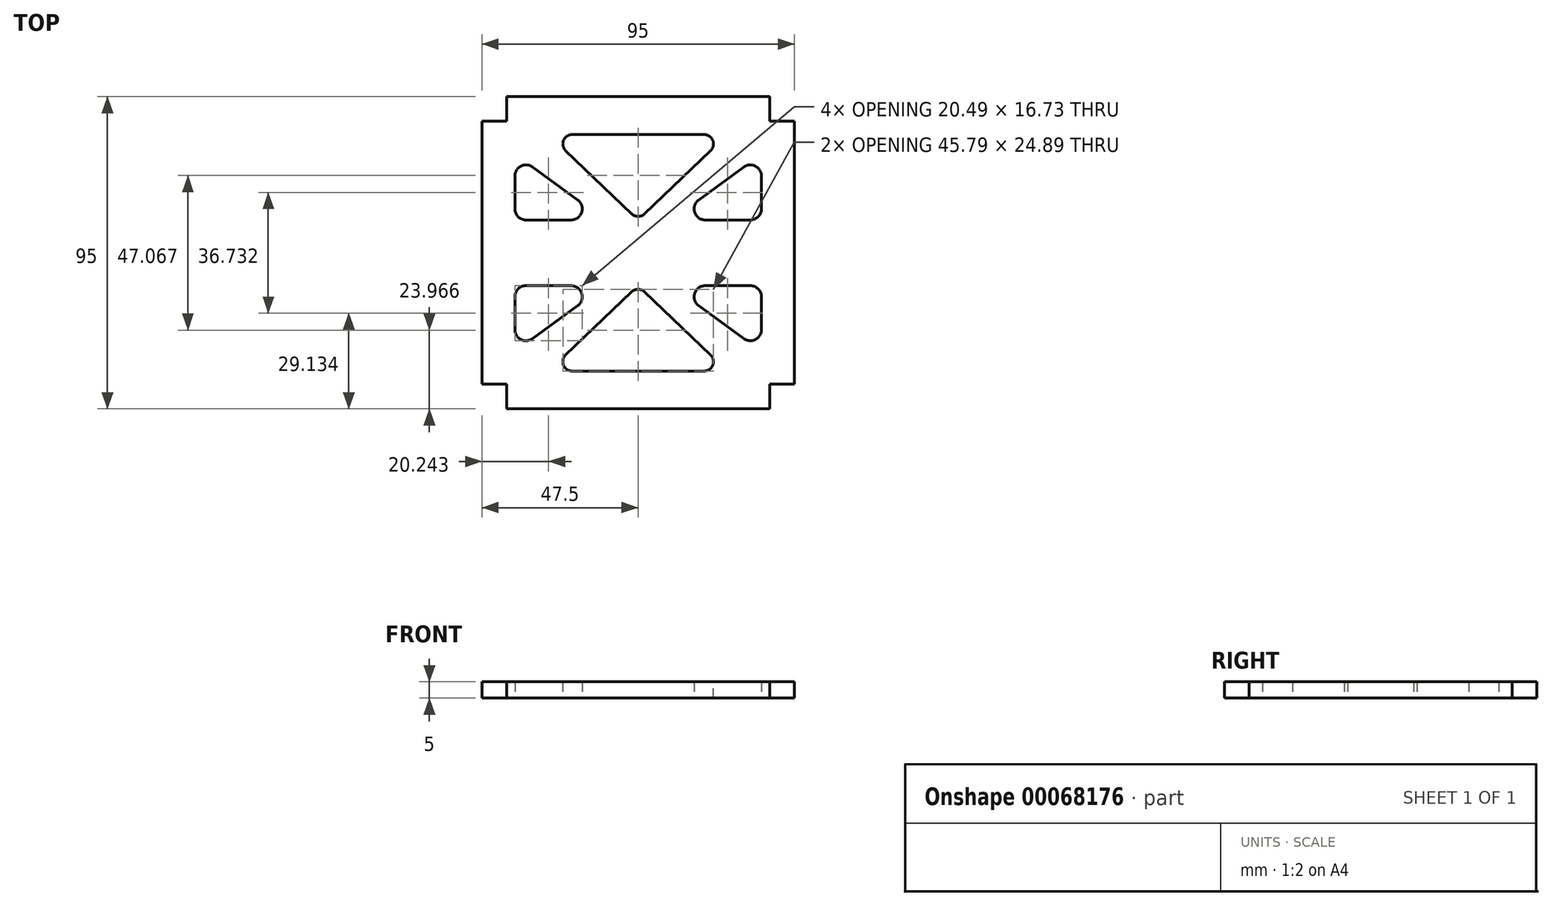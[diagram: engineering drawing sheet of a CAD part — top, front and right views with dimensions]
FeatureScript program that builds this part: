
annotation { "Feature Type Name" : "Feature", "Feature Type Description" : "" }
export const myFeature = defineFeature(function(context is Context, id is Id, definition is map)
    precondition{}
    {
        {
            var Q0;
            Q0=qCreatedBy(makeId("Top.planeOp"),FACE);
            var sketch = newSketch(context, id + "F0", { "sketchPlane" : qUnion([Q0])});
            skLineSegment(sketch, "E0.rect.bottom", {"start": v(40, -47.5) * mm, "end": v(-40, -47.5) * mm});
            skLineSegment(sketch, "E0.rect.top", {"start": v(40, 47.5) * mm, "end": v(-40, 47.5) * mm});
            skLineSegment(sketch, "E0.rect.left", {"start": v(47.5, -40) * mm, "end": v(47.5, 40) * mm});
            skLineSegment(sketch, "E0.rect.right", {"start": v(-47.5, -40) * mm, "end": v(-47.5, 40) * mm});
            skPoint(sketch, "E0.rect.middle", {"position": v(0, 0) * mm});
            skLineSegment(sketch, "E1.top", {"start": v(-47.5, 40) * mm, "end": v(-40, 40) * mm});
            skLineSegment(sketch, "E1.right", {"start": v(-40, 47.5) * mm, "end": v(-40, 40) * mm});
            skLineSegment(sketch, "E2.top", {"start": v(47.5, 40) * mm, "end": v(40, 40) * mm});
            skLineSegment(sketch, "E2.right", {"start": v(40, 47.5) * mm, "end": v(40, 40) * mm});
            skLineSegment(sketch, "E3.top", {"start": v(47.5, -40) * mm, "end": v(40, -40) * mm});
            skLineSegment(sketch, "E3.right", {"start": v(40, -47.5) * mm, "end": v(40, -40) * mm});
            skLineSegment(sketch, "E4.top", {"start": v(-47.5, -40) * mm, "end": v(-40, -40) * mm});
            skLineSegment(sketch, "E4.right", {"start": v(-40, -47.5) * mm, "end": v(-40, -40) * mm});
            skLineSegment(sketch, "E5", {"start": v(0, 0) * mm, "end": v(-22, 0) * mm, "construction": true});
            skLineSegment(sketch, "E6", {"start": v(0, 0) * mm, "end": v(22, 0) * mm, "construction": true});
            skLineSegment(sketch, "E7", {"start": v(-22, 0) * mm, "end": v(-22, -40) * mm, "construction": true});
            skLineSegment(sketch, "E8", {"start": v(22, 0) * mm, "end": v(22, -40) * mm, "construction": true});
            skLineSegment(sketch, "E9", {"start": v(-22, 0) * mm, "end": v(-22, -9) * mm});
            skLineSegment(sketch, "E10.rect.bottom", {"start": v(-27.14, 35.98) * mm, "end": v(27.14, 35.98) * mm});
            skLineSegment(sketch, "E11.rect.top", {"start": v(27.14, -35.98) * mm, "end": v(-27.14, -35.98) * mm});
            skLineSegment(sketch, "E12", {"start": v(0, -10) * mm, "end": v(-27.14, -35.98) * mm});
            skLineSegment(sketch, "E13", {"start": v(0, -10) * mm, "end": v(27.14, -35.98) * mm});
            skLineSegment(sketch, "E14", {"start": v(0, 10) * mm, "end": v(-27.14, 35.98) * mm});
            skLineSegment(sketch, "E15", {"start": v(0, 10) * mm, "end": v(27.14, 35.98) * mm});
            skLineSegment(sketch, "E16", {"start": v(0, 0) * mm, "end": v(0, 10) * mm, "construction": true});
            skLineSegment(sketch, "E17", {"start": v(0, 0) * mm, "end": v(0, -10) * mm, "construction": true});
            skLineSegment(sketch, "E18", {"start": v(0, 35.98) * mm, "end": v(0, 10) * mm, "construction": true});
            skLineSegment(sketch, "E19", {"start": v(0, 10) * mm, "end": v(10, 10) * mm, "construction": true});
            skLineSegment(sketch, "E20", {"start": v(47.5, 30) * mm, "end": v(37.5, 30) * mm, "construction": true});
            skLineSegment(sketch, "E21.bottom", {"start": v(10, 10) * mm, "end": v(37.5, 10) * mm});
            skLineSegment(sketch, "E21.right", {"start": v(37.5, 10) * mm, "end": v(37.5, 30) * mm});
            skLineSegment(sketch, "E22", {"start": v(10, 10) * mm, "end": v(37.5, 30) * mm});
            skLineSegment(sketch, "E23.top", {"start": v(-37.5, 10) * mm, "end": v(-10, 10) * mm});
            skLineSegment(sketch, "E23.left", {"start": v(-37.5, 30) * mm, "end": v(-37.5, 10) * mm});
            skLineSegment(sketch, "E24", {"start": v(-37.5, 30) * mm, "end": v(-10, 10) * mm});
            skLineSegment(sketch, "E25", {"start": v(37.5, -40) * mm, "end": v(37.5, -30) * mm, "construction": true});
            skLineSegment(sketch, "E26.bottom", {"start": v(10, -10) * mm, "end": v(37.5, -10) * mm});
            skLineSegment(sketch, "E26.right", {"start": v(37.5, -10) * mm, "end": v(37.5, -30) * mm});
            skLineSegment(sketch, "E27", {"start": v(10, -10) * mm, "end": v(37.5, -30) * mm});
            skLineSegment(sketch, "E28.top", {"start": v(-37.5, -10) * mm, "end": v(-10, -10) * mm});
            skLineSegment(sketch, "E28.left", {"start": v(-37.5, -30) * mm, "end": v(-37.5, -10) * mm});
            skLineSegment(sketch, "E29", {"start": v(-37.5, -30) * mm, "end": v(-10, -10) * mm});
            skSolve(sketch);
        }
        {
            var Q0;
            Q0=makeQuery(id+"F0.imprint","IMPRINT",FACE,{"disambiguationData":[TD([[makeQuery(id+"F0.imprint","IMPRINT",EDGE,{"derivedFrom":sQuery(id+"F0.wireOp",EDGE,"E0.rect.bottom")}),-1.0]])]});
            extrude(context, id + "F1", {"entities" : qUnion([Q0]), "depth" : 5 * mm});
        }
        {
            var Q0;
            Q0=makeQuery(id+"F1.opExtrude","SWEPT_EDGE",EDGE,{"disambiguationData":[OSD([sQuery(id+"F0.wireOp",EDGE,"E10.rect.bottom"),sQuery(id+"F0.wireOp",EDGE,"E15")])]});
            var Q1;
            Q1=makeQuery(id+"F1.opExtrude","SWEPT_EDGE",EDGE,{"disambiguationData":[OSD([sQuery(id+"F0.wireOp",EDGE,"E10.rect.bottom"),sQuery(id+"F0.wireOp",EDGE,"E14")])]});
            var Q2;
            Q2=makeQuery(id+"F1.opExtrude","SWEPT_EDGE",EDGE,{"disambiguationData":[OSD([sQuery(id+"F0.wireOp",EDGE,"E14"),sQuery(id+"F0.wireOp",EDGE,"E15")])]});
            var Q3;
            Q3=makeQuery(id+"F1.opExtrude","SWEPT_EDGE",EDGE,{"disambiguationData":[OSD([sQuery(id+"F0.wireOp",EDGE,"E12"),sQuery(id+"F0.wireOp",EDGE,"E13")])]});
            var Q4;
            Q4=makeQuery(id+"F1.opExtrude","SWEPT_EDGE",EDGE,{"disambiguationData":[OSD([sQuery(id+"F0.wireOp",EDGE,"E11.rect.top"),sQuery(id+"F0.wireOp",EDGE,"E12")])]});
            var Q5;
            Q5=makeQuery(id+"F1.opExtrude","SWEPT_EDGE",EDGE,{"disambiguationData":[OSD([sQuery(id+"F0.wireOp",EDGE,"E11.rect.top"),sQuery(id+"F0.wireOp",EDGE,"E13")])]});
            fillet(context, id + "F2", {"entities" : qUnion([Q0, Q1, Q2, Q3, Q4, Q5]), "radius" : 2.84 * mm, "tangentPropagation" : true, "allowEdgeOverflow" : false});
        }
        {
            var Q0;
            Q0=makeQuery(id+"F1.opExtrude","SWEPT_EDGE",EDGE,{"disambiguationData":[OSD([sQuery(id+"F0.wireOp",EDGE,"E21.right"),sQuery(id+"F0.wireOp",EDGE,"E22")])]});
            var Q1;
            Q1=makeQuery(id+"F1.opExtrude","SWEPT_EDGE",EDGE,{"disambiguationData":[OSD([sQuery(id+"F0.wireOp",EDGE,"E21.bottom"),sQuery(id+"F0.wireOp",EDGE,"E21.right")])]});
            var Q2;
            Q2=makeQuery(id+"F1.opExtrude","SWEPT_EDGE",EDGE,{"disambiguationData":[OSD([sQuery(id+"F0.wireOp",EDGE,"E26.bottom"),sQuery(id+"F0.wireOp",EDGE,"E27")])]});
            var Q3;
            Q3=makeQuery(id+"F1.opExtrude","SWEPT_EDGE",EDGE,{"disambiguationData":[OSD([sQuery(id+"F0.wireOp",EDGE,"E28.top"),sQuery(id+"F0.wireOp",EDGE,"E28.left")])]});
            var Q4;
            Q4=makeQuery(id+"F1.opExtrude","SWEPT_EDGE",EDGE,{"disambiguationData":[OSD([sQuery(id+"F0.wireOp",EDGE,"E28.top"),sQuery(id+"F0.wireOp",EDGE,"E29")])]});
            var Q5;
            Q5=makeQuery(id+"F1.opExtrude","SWEPT_EDGE",EDGE,{"disambiguationData":[OSD([sQuery(id+"F0.wireOp",EDGE,"E26.bottom"),sQuery(id+"F0.wireOp",EDGE,"E26.right")])]});
            var Q6;
            Q6=makeQuery(id+"F1.opExtrude","SWEPT_EDGE",EDGE,{"disambiguationData":[OSD([sQuery(id+"F0.wireOp",EDGE,"E23.left"),sQuery(id+"F0.wireOp",EDGE,"E24")])]});
            var Q7;
            Q7=makeQuery(id+"F1.opExtrude","SWEPT_EDGE",EDGE,{"disambiguationData":[OSD([sQuery(id+"F0.wireOp",EDGE,"E26.right"),sQuery(id+"F0.wireOp",EDGE,"E27")])]});
            var Q8;
            Q8=makeQuery(id+"F1.opExtrude","SWEPT_EDGE",EDGE,{"disambiguationData":[OSD([sQuery(id+"F0.wireOp",EDGE,"E23.top"),sQuery(id+"F0.wireOp",EDGE,"E24")])]});
            var Q9;
            Q9=makeQuery(id+"F1.opExtrude","SWEPT_EDGE",EDGE,{"disambiguationData":[OSD([sQuery(id+"F0.wireOp",EDGE,"E23.top"),sQuery(id+"F0.wireOp",EDGE,"E23.left")])]});
            var Q10;
            Q10=makeQuery(id+"F1.opExtrude","SWEPT_EDGE",EDGE,{"disambiguationData":[OSD([sQuery(id+"F0.wireOp",EDGE,"E28.left"),sQuery(id+"F0.wireOp",EDGE,"E29")])]});
            var Q11;
            Q11=makeQuery(id+"F1.opExtrude","SWEPT_EDGE",EDGE,{"disambiguationData":[OSD([sQuery(id+"F0.wireOp",EDGE,"E21.bottom"),sQuery(id+"F0.wireOp",EDGE,"E22")])]});
            fillet(context, id + "F3", {"entities" : qUnion([Q0, Q1, Q2, Q3, Q4, Q5, Q6, Q7, Q8, Q9, Q10, Q11]), "radius" : 3.38 * mm, "tangentPropagation" : true, "allowEdgeOverflow" : false});
        }
    });
